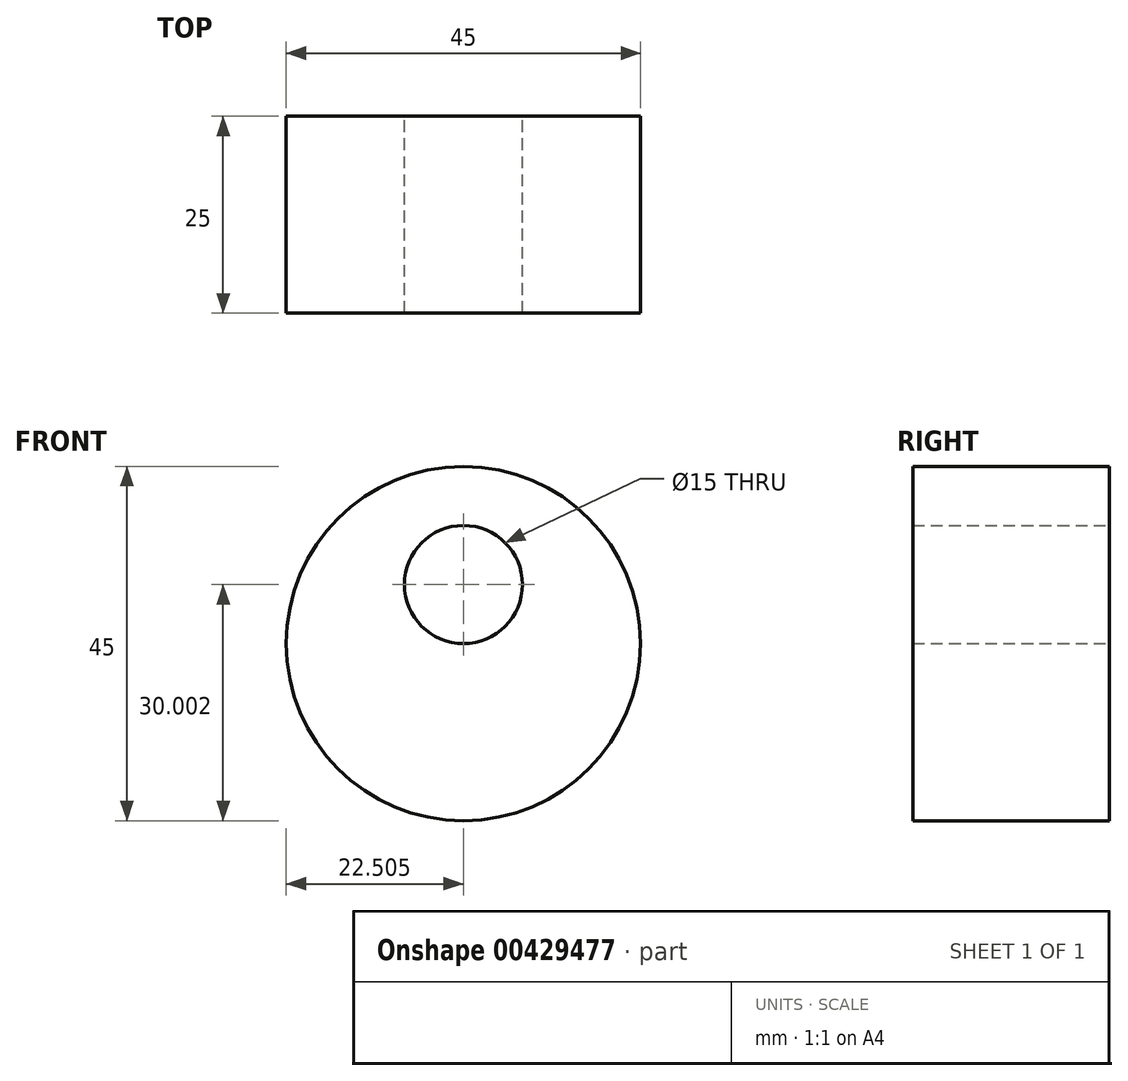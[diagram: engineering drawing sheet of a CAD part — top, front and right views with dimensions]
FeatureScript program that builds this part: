
annotation { "Feature Type Name" : "Feature", "Feature Type Description" : "" }
export const myFeature = defineFeature(function(context is Context, id is Id, definition is map)
    precondition{}
    {
        {
            var Q0;
            Q0=qCreatedBy(makeId("Front.planeOp"),FACE);
            var sketch = newSketch(context, id + "F0", { "sketchPlane" : qUnion([Q0])});
            skLineSegment(sketch, "E0.top", {"start": v(-49.4, 30.43) * mm, "end": v(-4.17, 30.43) * mm});
            skLineSegment(sketch, "E0.left", {"start": v(-49.4, 0) * mm, "end": v(-49.4, 30.43) * mm});
            skLineSegment(sketch, "E0.right", {"start": v(-4.17, 0) * mm, "end": v(-4.17, 30.43) * mm});
            skCircle(sketch, "E1", {"center": v(9.04, -4) * mm, "radius": 7.5 * mm});
            skCircle(sketch, "E2", {"center": v(9.04, -11.5) * mm, "radius": 22.5 * mm});
            skSolve(sketch);
        }
        {
            var Q0;
            Q0=makeQuery(id+"F0.imprint","IMPRINT",FACE,{"disambiguationData":[TD([[makeQuery(id+"F0.imprint","IMPRINT",EDGE,{"derivedFrom":sQuery(id+"F0.wireOp",EDGE,"E1")}),-1.0]])]});
            extrude(context, id + "F1", {"entities" : qUnion([Q0]), "depth" : 25 * mm});
        }
    });
